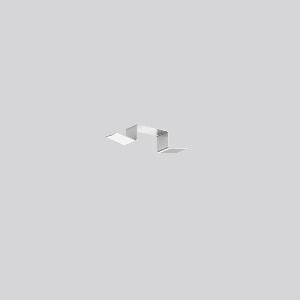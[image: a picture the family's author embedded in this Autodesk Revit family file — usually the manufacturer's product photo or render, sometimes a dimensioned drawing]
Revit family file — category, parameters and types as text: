
# Revit family: linedo_fixierklammer_982751_000_badc
name_source: partatom
category: Lighting Fixtures
units: mm (PartAtom-declared; Revit-internal decimal feet)

## family parameters
Cut with Voids When Loaded = No
Host = Face
Light Source = No
Part Type = Normal
Room Calculation Point = No
Round Connector Dimension = Use Diameter
Shared = No

## types (1)
- LINEDO Fixierklammer
    Apparent Load = 0 VA
    Default Elevation = 1800 mm
    Description = Fixing clamp. Spring steel, blank. For guiding external cables on top of the continuous line luminaire module.
Colour: stainless steel
Length: 10 mm
Width: 51 mm
Height: 10 mm
Weight: 2,6 g
Type of Installation: Recessed mounting, Surface mounting
    Height = 10 mm  [stored 0.0328084 ft]
    Lamp = 0 x
    Length = 10 mm  [stored 0.0328084 ft]
    Luminous efficacy = 0 lm/W
    Manufacturer = RZB
    ModVariant = No
    Model = 982751.000
    Mounting Place = Ceiling
    Mounting Type = Surface mounted
    Number of Poles = 1
    OnlyDefault = Yes
    Power Factor = 1
    Product Name = LINEDO Fixierklammer
    Product group = Surface mounted continuous line luminaire system
    ProductGroupID = 310
    Protection Class = Protection class
    Protection Degree = Degree of protection
    RLX_Detail_Level = 1
    RLX_Emergency_Light_Flux = 0 lm
    RLX_Emergency_Type = 0
    RLX_Emergency_Type_DB = No
    RlxData = <blob elided: 5413 chars, md5=f99336a9>
    Standby Power = 0 W
    System Light Flux = 0 lm
    System Power = 0 W
    Type Comments = Product without accessories
    Type Image = 982751.000.jpg
    URL = http://relux.com
    VarID = ---
    Voltage = 0 V
    Weight = 0.00 kg
    Width = 51 mm

note: [stored X ft] marks values corroborated as IEEE doubles in the binary element streams (Revit-internal decimal feet)

## geometry (parser evidence)
native form markers: Blend x2, Sweep x10
no freeform markers — native parametric forms only
